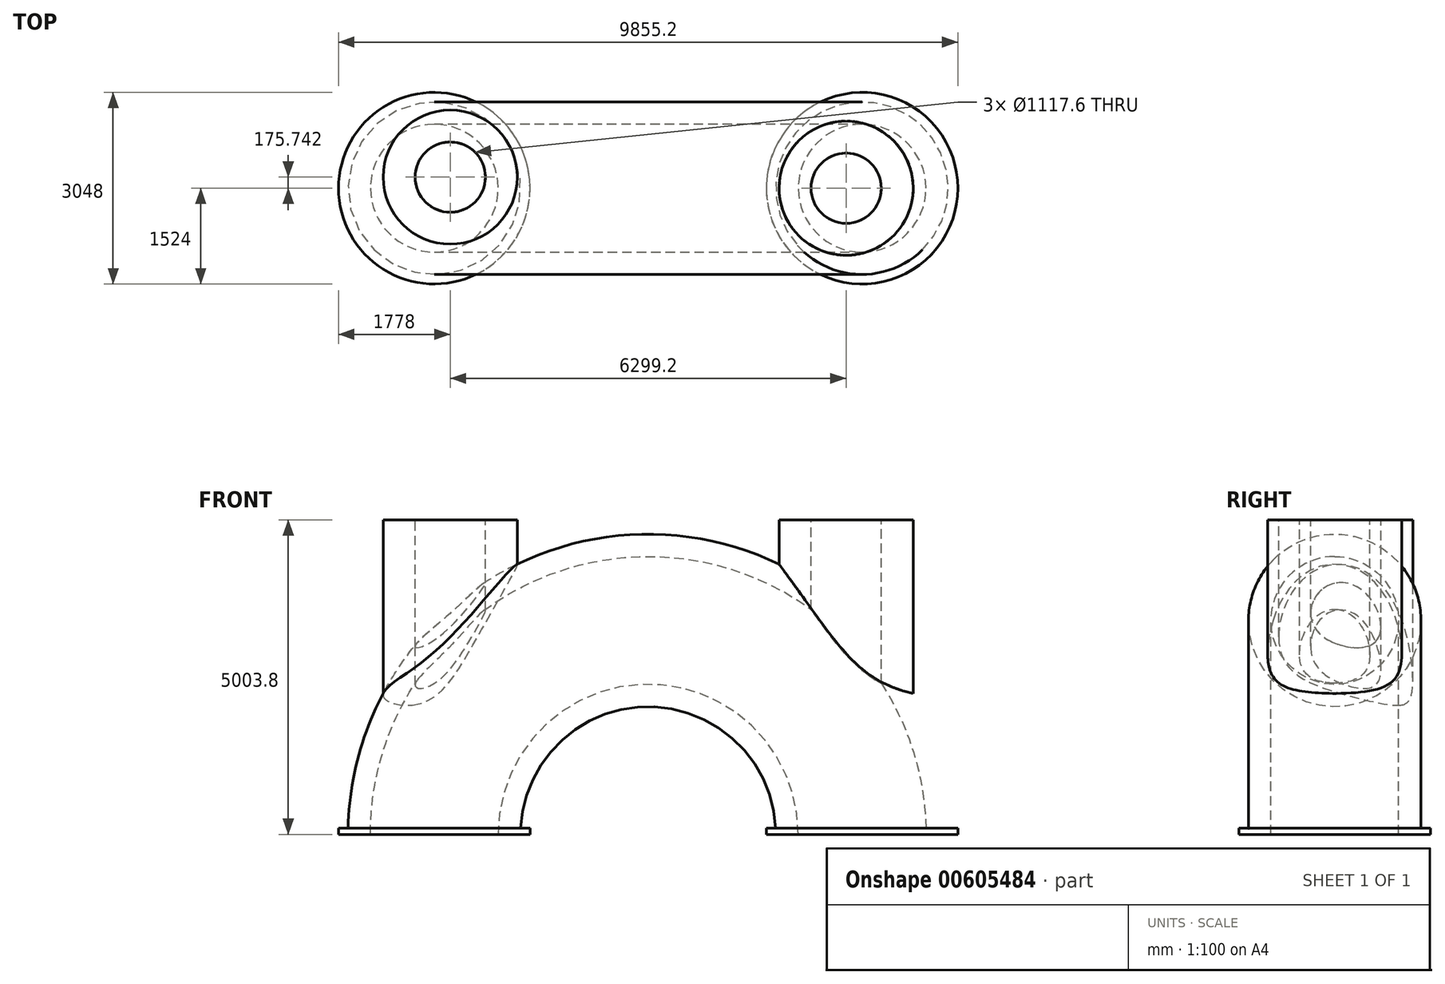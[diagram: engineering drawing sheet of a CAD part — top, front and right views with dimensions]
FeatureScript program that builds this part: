
annotation { "Feature Type Name" : "Feature", "Feature Type Description" : "" }
export const myFeature = defineFeature(function(context is Context, id is Id, definition is map)
    precondition{}
    {
        {
            var Q0;
            Q0=qCreatedBy(makeId("Front.planeOp"),FACE);
            var sketch = newSketch(context, id + "F0", { "sketchPlane" : qUnion([Q0])});
            skArc(sketch, "E0", {"start": v(3403.6, 0) * mm, "mid": v(0, 3403.6) * mm, "end": v(-3403.6, 0) * mm});
            skSolve(sketch);
        }
        {
            var Q0;
            Q0=qCreatedBy(makeId("Top.planeOp"),FACE);
            var Q1;
            Q1=sQuery(id+"F0.wireOp",VERTEX,"E0.end");
            cPlane(context, id + "F1", {"entities" : qUnion([Q0, Q1]), "cplaneType" : CPlaneType.PLANE_POINT, "offset" : 25.4 * mm, "width" : 152.4 * mm, "height" : 152.4 * mm});
        }
        {
            var Q0;
            Q0=qCreatedBy(id+"F1.planeOp",FACE);
            var sketch = newSketch(context, id + "F2", { "sketchPlane" : qUnion([Q0])});
            skCircle(sketch, "E1", {"center": v(-3403.6, 0) * mm, "radius": 1371.6 * mm});
            skSolve(sketch);
        }
        {
            var Q0;
            Q0=makeQuery(id+"F2.imprint","IMPRINT",FACE,{"disambiguationData":[TD([[makeQuery(id+"F2.imprint","IMPRINT",EDGE,{"derivedFrom":sQuery(id+"F2.wireOp",EDGE,"E1")}),1.0]])]});
            var Q1;
            Q1=sQuery(id+"F0.wireOp",EDGE,"E0");
            sweep(context, id + "F3", {"profiles" : qUnion([Q0]), "path" : qUnion([Q1])});
        }
        {
            var Q0;
            Q0=makeQuery(id+"F3.opSweep","CAP_FACE",FACE,{"disambiguationData":[OSD([sQuery(id+"F0.wireOp",VERTEX,"E0.end"),sQuery(id+"F2.wireOp",EDGE,"E1")])],"isStart":true});
            var sketch = newSketch(context, id + "F4", { "sketchPlane" : qUnion([Q0])});
            skCircle(sketch, "E2", {"center": v(-3403.6, 0) * mm, "radius": 1524 * mm});
            skCircle(sketch, "E3", {"center": v(3403.6, 0) * mm, "radius": 1524 * mm});
            skSolve(sketch);
        }
        {
            var Q0;
            Q0 = qSketchRegion(id + "F4", true);
            extrude(context, id + "F5", {"entities" : qUnion([Q0]), "operationType" : NewBodyOperationType.ADD, "oppositeDirection" : true, "depth" : 101.6 * mm, "offsetDistance" : 25.4 * mm});
        }
        {
            var Q0;
            Q0=makeQuery(id+"F5.boolean.opBoolean","MERGE",FACE,{"derivedFrom":[makeQuery(id+"F3.opSweep","CAP_FACE",FACE,{"disambiguationData":[OSD([sQuery(id+"F0.wireOp",VERTEX,"E0.start"),sQuery(id+"F2.wireOp",EDGE,"E1")])],"isStart":false}),makeQuery(id+"F5.opExtrude","CAP_FACE",FACE,{"disambiguationData":[OSD([sQuery(id+"F4.wireOp",EDGE,"E3")])],"isStart":true})]});
            cPlane(context, id + "F6", {"entities" : qUnion([Q0]), "cplaneType" : CPlaneType.OFFSET, "offset" : 5003.8 * mm, "oppositeDirection" : true, "width" : 152.4 * mm, "height" : 152.4 * mm});
        }
        {
            var Q0;
            Q0=qCreatedBy(id+"F6.planeOp",FACE);
            var sketch = newSketch(context, id + "F7", { "sketchPlane" : qUnion([Q0])});
            skCircle(sketch, "E4", {"center": v(3149.6, 0) * mm, "radius": 1066.8 * mm});
            skSolve(sketch);
        }
        {
            var Q0;
            Q0 = qSketchRegion(id + "F7", true);
            var Q1;
            Q1=makeQuery(id+"F3.opSweep","SWEPT_FACE",FACE,{"disambiguationData":[OSD([sQuery(id+"F0.wireOp",EDGE,"E0"),sQuery(id+"F2.wireOp",EDGE,"E1")])]});
            extrude(context, id + "F8", {"entities" : qUnion([Q0]), "operationType" : NewBodyOperationType.ADD, "endBound" : BoundingType.UP_TO_SURFACE, "depth" : 25.4 * mm, "endBoundEntityFace" : qUnion([Q1]), "offsetDistance" : 25.4 * mm});
        }
        {
            var Q0;
            Q0=makeQuery(id+"F5.boolean.opBoolean","MERGE",FACE,{"derivedFrom":[makeQuery(id+"F3.opSweep","CAP_FACE",FACE,{"disambiguationData":[OSD([sQuery(id+"F0.wireOp",VERTEX,"E0.end"),sQuery(id+"F2.wireOp",EDGE,"E1")])],"isStart":true}),makeQuery(id+"F5.opExtrude","CAP_FACE",FACE,{"disambiguationData":[OSD([sQuery(id+"F4.wireOp",EDGE,"E2")])],"isStart":true})]});
            var sketch = newSketch(context, id + "F9", { "sketchPlane" : qUnion([Q0])});
            skCircle(sketch, "E5", {"center": v(-3403.6, 0) * mm, "radius": 1016 * mm});
            skSolve(sketch);
        }
        {
            var Q0;
            Q0=makeQuery(id+"F9.imprint","IMPRINT",FACE,{"disambiguationData":[TD([[makeQuery(id+"F9.imprint","IMPRINT",EDGE,{"derivedFrom":sQuery(id+"F9.wireOp",EDGE,"E5")}),1.0]])]});
            var Q1;
            Q1 = qConstructionFilter(qBodyType(qCreatedBy(id + "F0" ,EDGE), BodyType.WIRE), ConstructionObject.NO);
            sweep(context, id + "F10", {"operationType" : NewBodyOperationType.REMOVE, "profiles" : qUnion([Q0]), "path" : qUnion([Q1])});
        }
        {
            var Q0;
            Q0=makeQuery(id+"F8.opExtrude","CAP_FACE",FACE,{"disambiguationData":[OSD([sQuery(id+"F7.wireOp",EDGE,"E4")])],"isStart":true});
            var sketch = newSketch(context, id + "F11", { "sketchPlane" : qUnion([Q0])});
            skPoint(sketch, "E6", {"position": v(3149.6, 0) * mm});
            skCircle(sketch, "E7", {"center": v(-3149.6, 175.74) * mm, "radius": 1066.8 * mm});
            skSolve(sketch);
        }
        {
            var Q0;
            Q0=sQuery(id+"F11.wireOp",VERTEX,"E6");
            var Q1;
            Q1=makeQuery(id+"F3.opSweep","SWEPT_BODY",BODY,{"disambiguationData":[OSD([sQuery(id+"F0.wireOp",EDGE,"E0"),sQuery(id+"F2.wireOp",EDGE,"E1")])]});
            hole(context, id + "F12", {"style" : HoleStyle.SIMPLE, "endStyle" : HoleEndStyle.THROUGH, "holeDiameter" : 1117.6 * mm, "majorDiameter" : 6.35 * mm, "isTappedThrough" : true, "tappedDepth" : 12.7 * mm, "tapClearance" : 3, "locations" : qUnion([Q0]), "scope" : qUnion([Q1])});
        }
        {
            var Q0;
            Q0=makeQuery(id+"F11.imprint","IMPRINT",FACE,{"disambiguationData":[TD([[makeQuery(id+"F11.imprint","IMPRINT",EDGE,{"derivedFrom":sQuery(id+"F11.wireOp",EDGE,"E7")}),1.0]])]});
            var Q1;
            Q1=makeQuery(id+"F3.opSweep","SWEPT_FACE",FACE,{"disambiguationData":[OSD([sQuery(id+"F0.wireOp",EDGE,"E0"),sQuery(id+"F2.wireOp",EDGE,"E1")])]});
            extrude(context, id + "F13", {"entities" : qUnion([Q0]), "endBound" : BoundingType.UP_TO_SURFACE, "oppositeDirection" : true, "depth" : 25.4 * mm, "endBoundEntityFace" : qUnion([Q1]), "offsetDistance" : 25.4 * mm});
        }
        {
            var Q0;
            Q0=sQuery(id+"F11.wireOp",VERTEX,"E7.center");
            var Q1;
            Q1=makeQuery(id+"F3.opSweep","SWEPT_BODY",BODY,{"disambiguationData":[OSD([sQuery(id+"F0.wireOp",EDGE,"E0"),sQuery(id+"F2.wireOp",EDGE,"E1")])]});
            var Q2;
            Q2=makeQuery(id+"F13.opExtrude","SWEPT_BODY",BODY,{"disambiguationData":[OSD([sQuery(id+"F11.wireOp",EDGE,"E7")])]});
            hole(context, id + "F14", {"style" : HoleStyle.SIMPLE, "endStyle" : HoleEndStyle.THROUGH, "holeDiameter" : 1117.6 * mm, "majorDiameter" : 6.35 * mm, "isTappedThrough" : true, "tappedDepth" : 12.7 * mm, "tapClearance" : 3, "locations" : qUnion([Q0]), "scope" : qUnion([Q1, Q2])});
        }
    });
